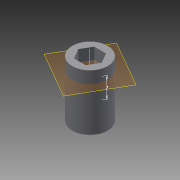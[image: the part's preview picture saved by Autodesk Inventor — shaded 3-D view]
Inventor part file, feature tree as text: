
AUTODESK INVENTOR PART (.ipt)
format: ipt  version: 2015 SP1 (Build 190203100, 203)  size: 196,608 bytes
history: native  units: mm
features: sketch x5, other x4, extrude x3, projected_geometry x2, plane x1, loft x1
ambient origin geometry x8: Origin, YZ Plane, XZ Plane, XY Plane, X Axis, Y Axis, Z Axis, Center Point
bodies: Body1 (feature_tree)
feature tree (16):
  other  "Sólido1"
  extrude  "Extrusión1"  Depth=1.0mm
  sketch  "Boceto2"  dims[d2=12.0mm d3=7.0mm d4=0.0mm]
  sketch  "Boceto3"  dims[d5=6.0mm d6=12.0mm d7=0.0mm]
  extrude  "Extrusión2"  Depth=7.0mm TaperAngle=0.0deg
  extrude  "Extrusión3"  Depth=12.0mm TaperAngle=0.0deg
  sketch  "Boceto4"  dims[d8=1.0mm d9=0.0mm d10=7.0mm]
  plane  "Plano de trabajo2"
  sketch  "Boceto5"  dims[d12=0.0mm d13=90.0deg d14=0.0mm d15=90.0deg d16=0.0mm d17=90.0deg]
  other  "Eje de trabajo2"
  loft  "Solevación1"
  sketch  "Boceto1"  dims[d0=4.0mm d1=1.0mm]
  projected_geometry  "Contorno proyectado1"
  projected_geometry  "Contorno proyectado2"
  other  "Aristas1"
  other  "Aristas2"
